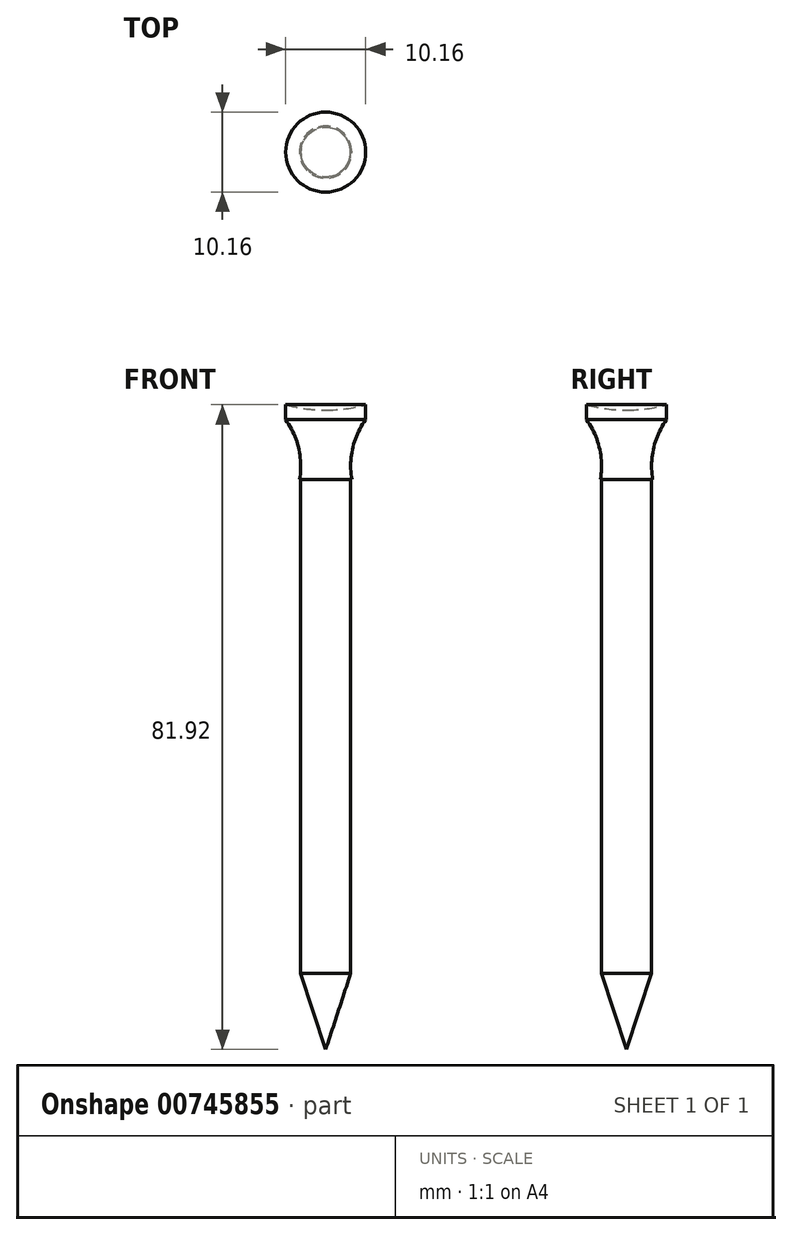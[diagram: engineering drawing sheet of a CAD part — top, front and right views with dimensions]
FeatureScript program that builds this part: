
annotation { "Feature Type Name" : "Feature", "Feature Type Description" : "" }
export const myFeature = defineFeature(function(context is Context, id is Id, definition is map)
    precondition{}
    {
        {
            var Q0;
            Q0=qCreatedBy(makeId("Front.planeOp"),FACE);
            var sketch = newSketch(context, id + "F0", { "sketchPlane" : qUnion([Q0])});
            skLineSegment(sketch, "E0.bottom", {"start": v(0, 0) * mm, "end": v(-3.18, 0) * mm});
            skLineSegment(sketch, "E0.left", {"start": v(0, 0) * mm, "end": v(0, -62.74) * mm});
            skLineSegment(sketch, "E0.right", {"start": v(-3.18, 0) * mm, "end": v(-3.17, -62.74) * mm});
            skLineSegment(sketch, "E1", {"start": v(-3.17, -62.74) * mm, "end": v(0, -72.4) * mm});
            skLineSegment(sketch, "E2", {"start": v(0, -62.74) * mm, "end": v(0, -72.4) * mm});
            skSolve(sketch);
        }
        {
            var Q0;
            Q0=makeQuery(id+"F0.imprint","IMPRINT",FACE,{"disambiguationData":[TD([[makeQuery(id+"F0.imprint","IMPRINT",EDGE,{"derivedFrom":sQuery(id+"F0.wireOp",EDGE,"E0.bottom")}),1.0]])]});
            var Q1;
            Q1=makeQuery(id+"F0.imprint","IMPRINT",FACE,{"disambiguationData":[TD([[makeQuery(id+"F0.imprint","IMPRINT",EDGE,{"derivedFrom":sQuery(id+"F0.wireOp",EDGE,"E0.top")}),1.0]])]});
            var Q2;
            Q2=sQuery(id+"F0.wireOp",EDGE,"E0.left");
            revolve(context, id + "F1", {"surfaceOperationType" : NewSurfaceOperationType.NEW, "entities" : qUnion([Q0, Q1]), "axis" : qUnion([Q2]), "revolveType" : RevolveType.FULL});
        }
        {
            var Q0;
            Q0=qCreatedBy(makeId("Front.planeOp"),FACE);
            var sketch = newSketch(context, id + "F2", { "sketchPlane" : qUnion([Q0])});
            skArc(sketch, "E3", {"start": v(-3.32, 0) * mm, "mid": v(-3.44, 3.99) * mm, "end": v(-5.08, 7.62) * mm});
            skLineSegment(sketch, "E4", {"start": v(0, 0) * mm, "end": v(0, 7.62) * mm});
            skLineSegment(sketch, "E5", {"start": v(0, 7.62) * mm, "end": v(-5.08, 7.62) * mm});
            skLineSegment(sketch, "E6", {"start": v(0, 0) * mm, "end": v(-3.32, 0) * mm});
            skLineSegment(sketch, "E7", {"start": v(-5.08, 7.62) * mm, "end": v(-5.08, 9.53) * mm});
            skArc(sketch, "E8", {"start": v(-5.08, 9.53) * mm, "mid": v(-2.56, 9) * mm, "end": v(0, 8.84) * mm});
            skLineSegment(sketch, "E9", {"start": v(0, 7.62) * mm, "end": v(0, 8.84) * mm});
            skPoint(sketch, "E10.orphan", {"position": v(5.08, 9.53) * mm});
            skSolve(sketch);
        }
        {
            var Q0;
            Q0=makeQuery(id+"F2.imprint","IMPRINT",FACE,{"disambiguationData":[TD([[makeQuery(id+"F2.imprint","IMPRINT",EDGE,{"derivedFrom":sQuery(id+"F2.wireOp",EDGE,"E3")}),-1.0]])]});
            var Q1;
            Q1=makeQuery(id+"F2.imprint","IMPRINT",FACE,{"disambiguationData":[TD([[makeQuery(id+"F2.imprint","IMPRINT",EDGE,{"derivedFrom":sQuery(id+"F2.wireOp",EDGE,"E5")}),-1.0]])]});
            var Q2;
            Q2=sQuery(id+"F2.wireOp",EDGE,"E9");
            revolve(context, id + "F3", {"operationType" : NewBodyOperationType.ADD, "surfaceOperationType" : NewSurfaceOperationType.NEW, "entities" : qUnion([Q0, Q1]), "axis" : qUnion([Q2]), "revolveType" : RevolveType.FULL});
        }
    });
